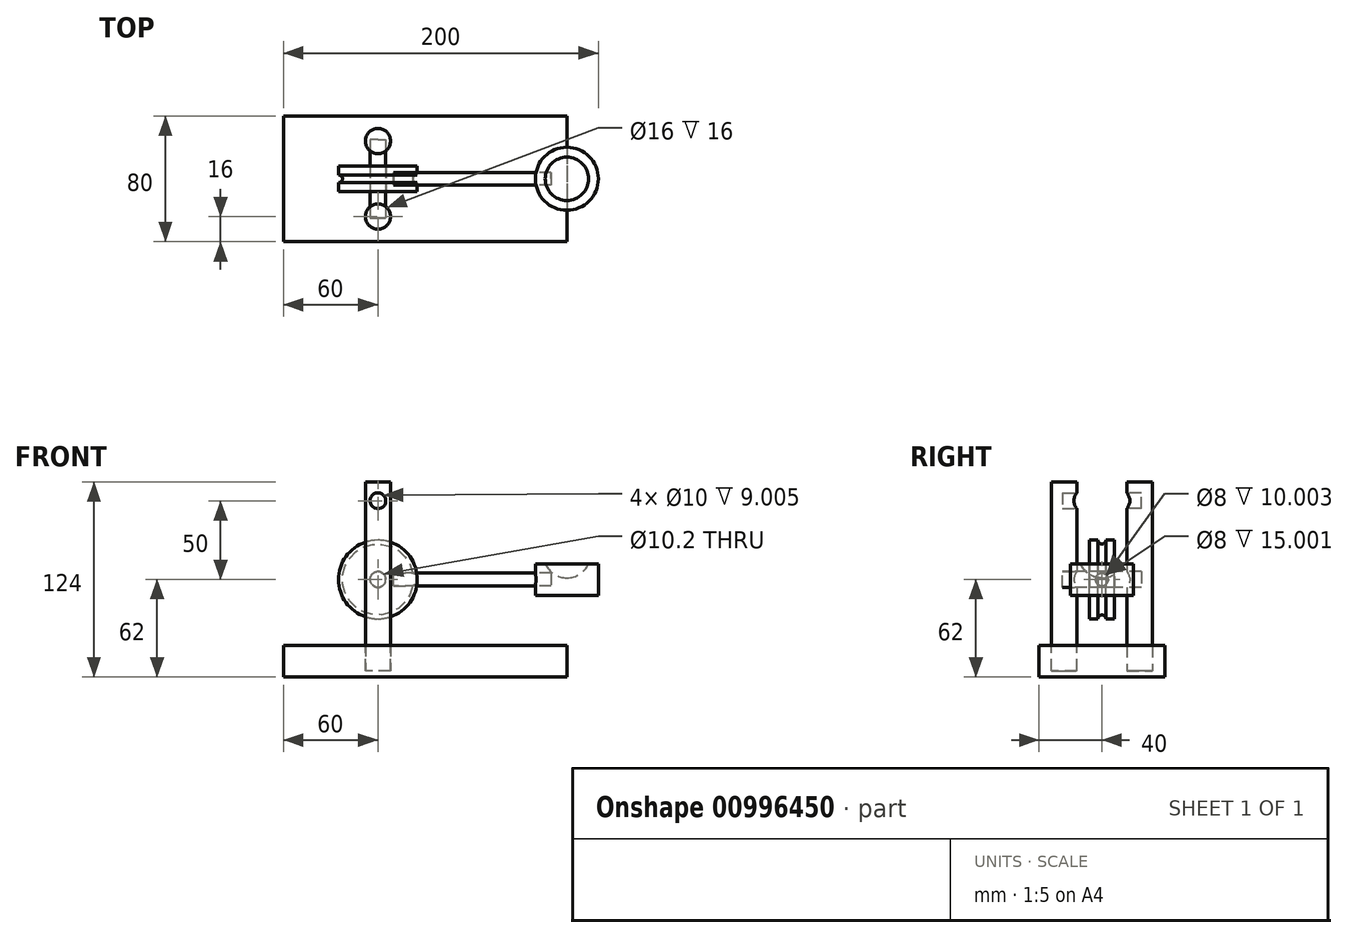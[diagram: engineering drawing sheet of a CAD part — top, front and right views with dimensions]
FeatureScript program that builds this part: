
annotation { "Feature Type Name" : "Feature", "Feature Type Description" : "" }
export const myFeature = defineFeature(function(context is Context, id is Id, definition is map)
    precondition{}
    {
        {
            var Q0;
            Q0=qCreatedBy(makeId("Top.planeOp"),FACE);
            var sketch = newSketch(context, id + "F0", { "sketchPlane" : qUnion([Q0])});
            skLineSegment(sketch, "E0.bottom", {"start": v(90, 40) * mm, "end": v(-90, 40) * mm});
            skLineSegment(sketch, "E0.top", {"start": v(90, -40) * mm, "end": v(-90, -40) * mm});
            skLineSegment(sketch, "E0.left", {"start": v(90, 40) * mm, "end": v(90, -40) * mm});
            skLineSegment(sketch, "E0.right", {"start": v(-90, 40) * mm, "end": v(-90, -40) * mm});
            skPoint(sketch, "E0.middle", {"position": v(0, 0) * mm});
            skSolve(sketch);
        }
        {
            var Q0;
            Q0 = qSketchRegion(id + "F0", true);
            extrude(context, id + "F1", {"entities" : qUnion([Q0]), "depth" : 20 * mm, "offsetDistance" : 25 * mm});
        }
        {
            var Q0;
            Q0=makeQuery(id+"F1.opExtrude","CAP_FACE",FACE,{"disambiguationData":[OSD([sQuery(id+"F0.wireOp",EDGE,"E0.bottom"),sQuery(id+"F0.wireOp",EDGE,"E0.top"),sQuery(id+"F0.wireOp",EDGE,"E0.left"),sQuery(id+"F0.wireOp",EDGE,"E0.right")])],"isStart":false});
            var sketch = newSketch(context, id + "F2", { "sketchPlane" : qUnion([Q0])});
            skCircle(sketch, "E1", {"center": v(-30, -24) * mm, "radius": 8 * mm});
            skSolve(sketch);
        }
        {
            var Q0;
            Q0 = qSketchRegion(id + "F2", true);
            extrude(context, id + "F3", {"entities" : qUnion([Q0]), "operationType" : NewBodyOperationType.REMOVE, "oppositeDirection" : true, "depth" : 16 * mm, "offsetDistance" : 25 * mm});
        }
        {
            var Q0;
            Q0=makeQuery(id+"F3.boolean.opBoolean","COPY",FACE,{"derivedFrom":makeQuery(id+"F3.opExtrude","CAP_FACE",FACE,{"disambiguationData":[OSD([sQuery(id+"F2.wireOp",EDGE,"E1")])],"isStart":false})});
            var sketch = newSketch(context, id + "F4", { "sketchPlane" : qUnion([Q0])});
            skCircle(sketch, "E2.0", {"center": v(-30, -24) * mm, "radius": 8 * mm});
            skSolve(sketch);
        }
        {
            var Q0;
            Q0 = qSketchRegion(id + "F4", true);
            extrude(context, id + "F5", {"entities" : qUnion([Q0]), "depth" : 120 * mm, "offsetDistance" : 25 * mm});
        }
        {
            var Q0;
            Q0=qCreatedBy(makeId("Front.planeOp"),FACE);
            var sketch = newSketch(context, id + "F6", { "sketchPlane" : qUnion([Q0])});
            skCircle(sketch, "E3", {"center": v(-30, 112) * mm, "radius": 5 * mm});
            skCircle(sketch, "E4", {"center": v(-30, 62) * mm, "radius": 5 * mm});
            skSolve(sketch);
        }
        {
            var Q0;
            Q0 = qSketchRegion(id + "F6", true);
            extrude(context, id + "F7", {"entities" : qUnion([Q0]), "operationType" : NewBodyOperationType.REMOVE, "depth" : 25 * mm, "offsetDistance" : 25 * mm});
        }
        {
            var Q0;
            Q0=makeQuery(id+"F5.opExtrude","SWEPT_BODY",BODY,{"disambiguationData":[OSD([sQuery(id+"F4.wireOp",EDGE,"E2.0")])]});
            var Q1;
            Q1=qCreatedBy(makeId("Front.planeOp"),FACE);
            mirror(context, id + "F8", {"entities" : qUnion([Q0]), "mirrorPlane" : qUnion([Q1])});
        }
        {
            var Q0;
            Q0=makeQuery(id+"F7.boolean.opBoolean","COPY",FACE,{"derivedFrom":makeQuery(id+"F7.opExtrude","CAP_FACE",FACE,{"disambiguationData":[OSD([sQuery(id+"F6.wireOp",EDGE,"E4")])],"isStart":false})});
            var sketch = newSketch(context, id + "F9", { "sketchPlane" : qUnion([Q0])});
            skCircle(sketch, "E5.0", {"center": v(30, 62) * mm, "radius": 5 * mm});
            skSolve(sketch);
        }
        {
            var Q0;
            Q0 = qSketchRegion(id + "F9", true);
            var Q1;
            Q1=makeQuery(id+"F8.opPattern","COPY",FACE,{"derivedFrom":makeQuery(id+"F7.boolean.opBoolean","COPY",FACE,{"derivedFrom":makeQuery(id+"F7.opExtrude","CAP_FACE",FACE,{"disambiguationData":[OSD([sQuery(id+"F6.wireOp",EDGE,"E4")])],"isStart":false})}),"instanceName":"1"});
            extrude(context, id + "F10", {"entities" : qUnion([Q0]), "endBound" : BoundingType.UP_TO_SURFACE, "depth" : 25 * mm, "endBoundEntityFace" : qUnion([Q1]), "offsetDistance" : 25 * mm});
        }
        {
            var Q0;
            Q0=qCreatedBy(makeId("Right.planeOp"),FACE);
            cPlane(context, id + "F11", {"entities" : qUnion([Q0]), "cplaneType" : CPlaneType.OFFSET, "offset" : 30 * mm, "oppositeDirection" : true, "width" : 150 * mm, "height" : 150 * mm});
        }
        {
            var Q0;
            Q0=qCreatedBy(id+"F11.planeOp",FACE);
            var sketch = newSketch(context, id + "F12", { "sketchPlane" : qUnion([Q0])});
            skLineSegment(sketch, "E6", {"start": v(0, 62) * mm, "end": v(0, 89.83) * mm, "construction": true});
            skLineSegment(sketch, "E7", {"start": v(-25.7, 62) * mm, "end": v(0, 62) * mm, "construction": true});
            skLineSegment(sketch, "E8", {"start": v(0, 67.1) * mm, "end": v(-8, 67.1) * mm});
            skLineSegment(sketch, "E9", {"start": v(-8, 67.1) * mm, "end": v(-8, 87) * mm});
            skLineSegment(sketch, "E10", {"start": v(-8, 87) * mm, "end": v(-2.5, 87) * mm});
            skArc(sketch, "E11", {"start": v(-2.5, 87) * mm, "mid": v(-1.77, 85.23) * mm, "end": v(0, 84.5) * mm});
            skLineSegment(sketch, "E12.MirrorCS", {"start": v(8, 67.1) * mm, "end": v(8, 87) * mm});
            skLineSegment(sketch, "E13.MirrorCS", {"start": v(8, 87) * mm, "end": v(2.5, 87) * mm});
            skLineSegment(sketch, "E14.MirrorCS", {"start": v(0, 67.1) * mm, "end": v(8, 67.1) * mm});
            skArc(sketch, "E15.MirrorCS", {"start": v(2.5, 87) * mm, "mid": v(1.77, 85.23) * mm, "end": v(0, 84.5) * mm});
            skSolve(sketch);
        }
        {
            var Q0;
            Q0 = qSketchRegion(id + "F12", true);
            var Q1;
            Q1=sQuery(id+"F12.wireOp",EDGE,"E7");
            revolve(context, id + "F13", {"surfaceOperationType" : NewSurfaceOperationType.NEW, "entities" : qUnion([Q0]), "axis" : qUnion([Q1]), "revolveType" : RevolveType.FULL});
        }
        {
            var Q0;
            Q0=qCreatedBy(makeId("Right.planeOp"),FACE);
            var sketch = newSketch(context, id + "F14", { "sketchPlane" : qUnion([Q0])});
            skCircle(sketch, "E16", {"center": v(0, 62) * mm, "radius": 4 * mm});
            skSolve(sketch);
        }
        {
            var Q0;
            Q0 = qSketchRegion(id + "F14", true);
            extrude(context, id + "F15", {"entities" : qUnion([Q0]), "operationType" : NewBodyOperationType.REMOVE, "oppositeDirection" : true, "depth" : 20 * mm, "offsetDistance" : 25 * mm});
        }
        {
            var Q0;
            Q0=makeQuery(id+"F15.boolean.opBoolean","COPY",FACE,{"derivedFrom":makeQuery(id+"F15.opExtrude","CAP_FACE",FACE,{"disambiguationData":[OSD([sQuery(id+"F14.wireOp",EDGE,"E16")])],"isStart":false})});
            var sketch = newSketch(context, id + "F16", { "sketchPlane" : qUnion([Q0])});
            skCircle(sketch, "E17.0", {"center": v(0, 62) * mm, "radius": 4 * mm});
            skSolve(sketch);
        }
        {
            var Q0;
            Q0 = qSketchRegion(id + "F16", true);
            extrude(context, id + "F17", {"entities" : qUnion([Q0]), "depth" : 100 * mm, "offsetDistance" : 25 * mm});
        }
        {
            var Q0;
            Q0=qCreatedBy(makeId("Top.planeOp"),FACE);
            cPlane(context, id + "F18", {"entities" : qUnion([Q0]), "cplaneType" : CPlaneType.OFFSET, "offset" : 62 * mm, "width" : 150 * mm, "height" : 150 * mm});
        }
        {
            var Q0;
            Q0=qCreatedBy(id+"F18.planeOp",FACE);
            var sketch = newSketch(context, id + "F19", { "sketchPlane" : qUnion([Q0])});
            skCircle(sketch, "E18", {"center": v(90, 0) * mm, "radius": 20 * mm});
            skSolve(sketch);
        }
        {
            var Q0;
            Q0 = qSketchRegion(id + "F19", true);
            extrude(context, id + "F20", {"entities" : qUnion([Q0]), "depth" : 10 * mm, "offsetDistance" : 25 * mm, "hasSecondDirection" : true, "secondDirectionOppositeDirection" : true, "secondDirectionDepth" : 10 * mm});
        }
        {
            var Q0;
            Q0=makeQuery(id+"F17.opExtrude","SWEPT_BODY",BODY,{"disambiguationData":[OSD([sQuery(id+"F16.wireOp",EDGE,"E17.0")])]});
            var Q1;
            Q1=makeQuery(id+"F20.opExtrude","SWEPT_BODY",BODY,{"disambiguationData":[OSD([sQuery(id+"F19.wireOp",EDGE,"E18")])]});
            booleanBodies(context, id + "F21", {"operationType" : BooleanOperationType.SUBTRACTION, "tools" : qUnion([Q0]), "targets" : qUnion([Q1]), "keepTools" : true});
        }
        {
            var Q0;
            Q0=makeQuery(id+"F20.opExtrude","CAP_FACE",FACE,{"disambiguationData":[OSD([sQuery(id+"F19.wireOp",EDGE,"E18")])],"isStart":false});
            var sketch = newSketch(context, id + "F22", { "sketchPlane" : qUnion([Q0])});
            skPoint(sketch, "E19", {"position": v(90, 0) * mm});
            skSolve(sketch);
        }
        {
            var Q0;
            Q0=qCreatedBy(id+"F11.planeOp",FACE);
            var Q1;
            Q1=sQuery(id+"F22.wireOp",VERTEX,"E19");
            cPlane(context, id + "F23", {"entities" : qUnion([Q0, Q1]), "cplaneType" : CPlaneType.PLANE_POINT, "offset" : 25 * mm, "width" : 150 * mm, "height" : 150 * mm});
        }
        {
            var Q0;
            Q0=qCreatedBy(id+"F23.planeOp",FACE);
            var sketch = newSketch(context, id + "F24", { "sketchPlane" : qUnion([Q0])});
            skArc(sketch, "E20", {"start": v(0, 63) * mm, "mid": v(15, 78) * mm, "end": v(0, 93) * mm});
            skLineSegment(sketch, "E21", {"start": v(0, 63) * mm, "end": v(0, 93) * mm});
            skPoint(sketch, "E22.orphan", {"position": v(0, 72.32) * mm});
            skLineSegment(sketch, "E23", {"start": v(0, 33.52) * mm, "end": v(0, 111.65) * mm, "construction": true});
            skSolve(sketch);
        }
        {
            var Q0;
            Q0 = qSketchRegion(id + "F24", true);
            var Q1;
            Q1=sQuery(id+"F24.wireOp",EDGE,"E23");
            revolve(context, id + "F25", {"operationType" : NewBodyOperationType.REMOVE, "surfaceOperationType" : NewSurfaceOperationType.NEW, "entities" : qUnion([Q0]), "axis" : qUnion([Q1]), "revolveType" : RevolveType.FULL, "oppositeDirection" : true});
        }
    });
